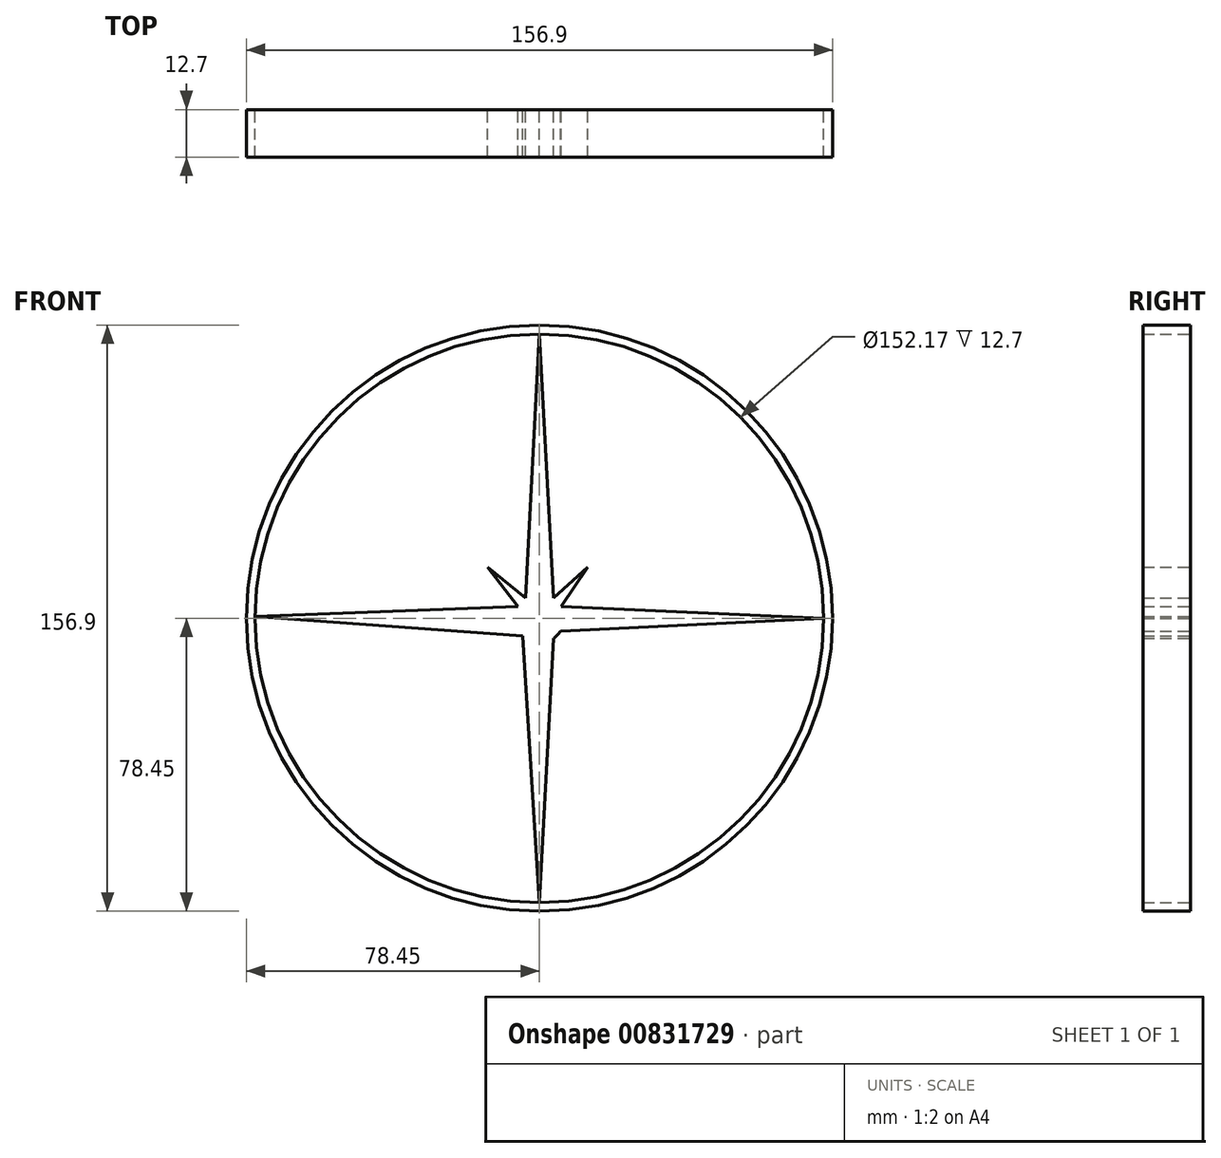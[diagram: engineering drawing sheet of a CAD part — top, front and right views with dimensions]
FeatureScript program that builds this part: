
annotation { "Feature Type Name" : "Feature", "Feature Type Description" : "" }
export const myFeature = defineFeature(function(context is Context, id is Id, definition is map)
    precondition{}
    {
        {
            var Q0;
            Q0=qCreatedBy(makeId("Front.planeOp"),FACE);
            var sketch = newSketch(context, id + "F0", { "sketchPlane" : qUnion([Q0])});
            skCircle(sketch, "E0", {"center": v(0, 0) * mm, "radius": 76.09 * mm});
            skCircle(sketch, "E1", {"center": v(0, 0) * mm, "radius": 78.45 * mm});
            skLineSegment(sketch, "E2", {"start": v(76.09, 0) * mm, "end": v(5.63, -3.45) * mm});
            skLineSegment(sketch, "E3", {"start": v(76.09, 0) * mm, "end": v(5.8, 3.15) * mm});
            skLineSegment(sketch, "E4", {"start": v(-3.77, 5.43) * mm, "end": v(0, 76.09) * mm});
            skLineSegment(sketch, "E5", {"start": v(0, 76.09) * mm, "end": v(3.77, 5.43) * mm});
            skLineSegment(sketch, "E6", {"start": v(-4.54, -4.8) * mm, "end": v(0, -76.09) * mm});
            skLineSegment(sketch, "E7", {"start": v(0, -76.09) * mm, "end": v(3.77, -5.43) * mm});
            skArc(sketch, "E8.trimOffspring", {"start": v(3.77, -5.43) * mm, "mid": v(4.8, -4.54) * mm, "end": v(5.63, -3.45) * mm});
            skLineSegment(sketch, "E9", {"start": v(-5.8, 3.15) * mm, "end": v(-76.08, 0.5) * mm});
            skPoint(sketch, "E9.endSnap0", {"position": v(-6.59, 0.5) * mm});
            skLineSegment(sketch, "E10", {"start": v(-76.08, 0.5) * mm, "end": v(-4.54, -4.8) * mm});
            skLineSegment(sketch, "E11", {"start": v(-3.77, 5.43) * mm, "end": v(-13.84, 13.65) * mm});
            skLineSegment(sketch, "E12", {"start": v(-13.84, 13.65) * mm, "end": v(-5.8, 3.15) * mm});
            skLineSegment(sketch, "E13", {"start": v(3.77, 5.43) * mm, "end": v(12.95, 13.65) * mm});
            skLineSegment(sketch, "E14", {"start": v(12.95, 13.65) * mm, "end": v(5.8, 3.15) * mm});
            skPoint(sketch, "E15.start.orphan", {"position": v(-5.8, -4.8) * mm});
            skSolve(sketch);
        }
        {
            var Q0;
            Q0=makeQuery(id+"F0.imprint","IMPRINT",FACE,{"disambiguationData":[TD([[makeQuery(id+"F0.imprint","IMPRINT",EDGE,{"derivedFrom":sQuery(id+"F0.wireOp",EDGE,"E2")}),-1.0]])]});
            var Q1;
            Q1=makeQuery(id+"F0.imprint","IMPRINT",FACE,{"disambiguationData":[TD([[makeQuery(id+"F0.imprint","IMPRINT",EDGE,{"derivedFrom":sQuery(id+"F0.wireOp",EDGE,"E1")}),1.0]])]});
            extrude(context, id + "F1", {"entities" : qUnion([Q0, Q1]), "depth" : 12.7 * mm, "offsetDistance" : 25.4 * mm});
        }
    });
